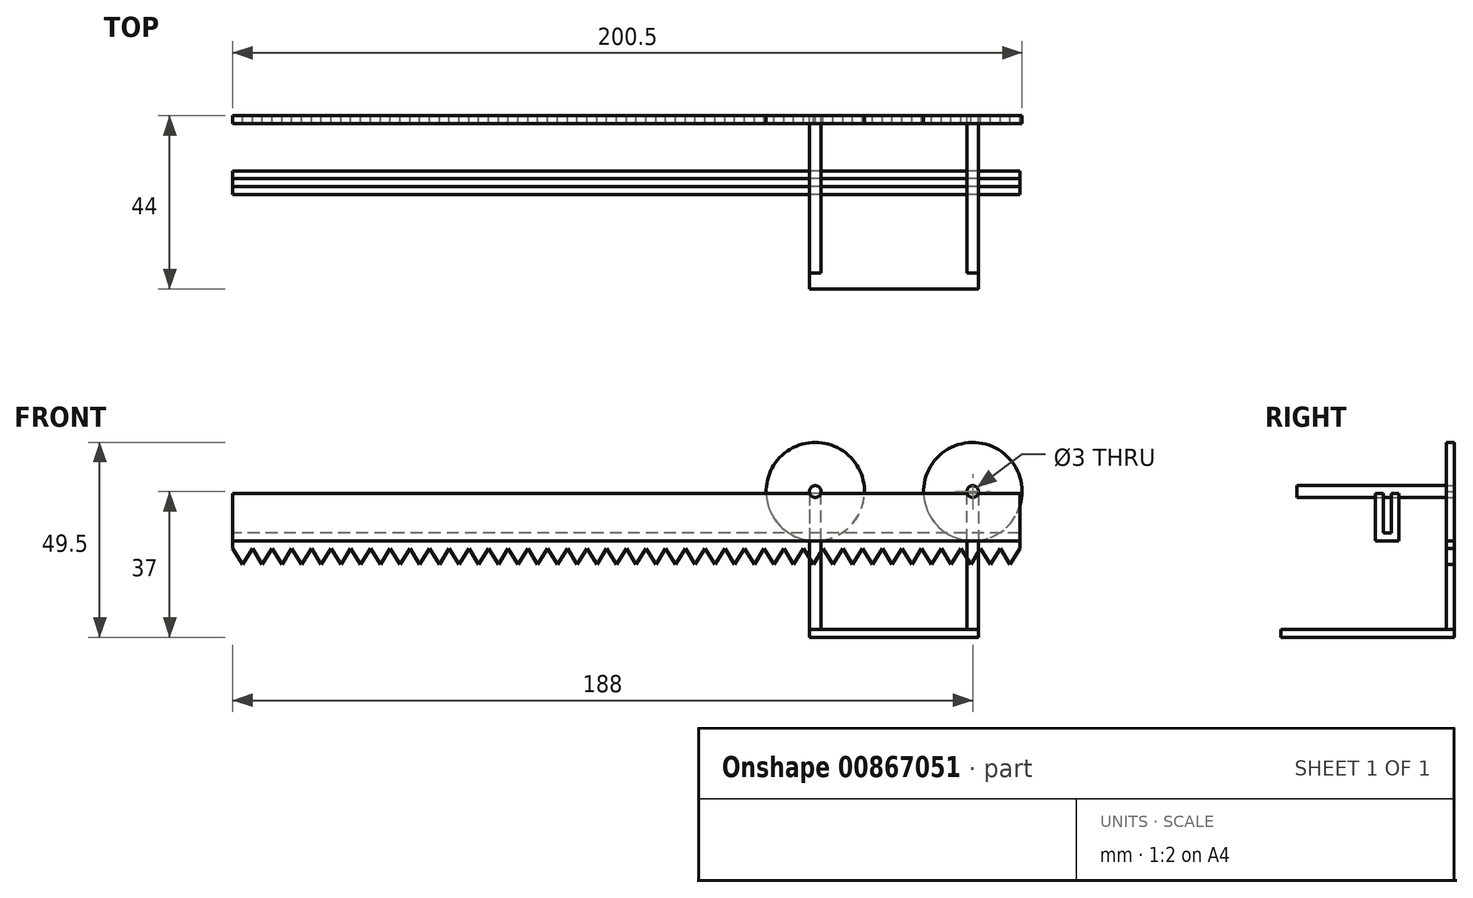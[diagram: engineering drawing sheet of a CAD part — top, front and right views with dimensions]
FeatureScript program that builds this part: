
annotation { "Feature Type Name" : "Feature", "Feature Type Description" : "" }
export const myFeature = defineFeature(function(context is Context, id is Id, definition is map)
    precondition{}
    {
        {
            assignVariable(context, id + "F0", {"name" : "Length", "anyValue" : 200});
        }
        {
            assignVariable(context, id + "F1", {"name" : "Width_Of_Cart", "anyValue" : 40});
        }
        {
            var Q0;
            Q0=qCreatedBy(makeId("Right.planeOp"),FACE);
            var sketch = newSketch(context, id + "F2", { "sketchPlane" : qUnion([Q0])});
            skLineSegment(sketch, "E0", {"start": v(-14, 0) * mm, "end": v(-14, 12) * mm});
            skLineSegment(sketch, "E1", {"start": v(-14, 12) * mm, "end": v(-16, 12) * mm});
            skLineSegment(sketch, "E2", {"start": v(-16, 12) * mm, "end": v(-16, 2) * mm});
            skLineSegment(sketch, "E3", {"start": v(-16, 2) * mm, "end": v(-18, 2) * mm});
            skLineSegment(sketch, "E4", {"start": v(-18, 2) * mm, "end": v(-18, 12) * mm});
            skLineSegment(sketch, "E5", {"start": v(-18, 12) * mm, "end": v(-20, 12) * mm});
            skLineSegment(sketch, "E6", {"start": v(-20, 12) * mm, "end": v(-20, 0) * mm});
            skLineSegment(sketch, "E7", {"start": v(-20, 0) * mm, "end": v(-14, 0) * mm});
            skLineSegment(sketch, "E8", {"start": v(-17, 2) * mm, "end": v(-17, 12) * mm, "construction": true});
            skLineSegment(sketch, "E9", {"start": v(0, 0.92) * mm, "end": v(0, 20.43) * mm, "construction": true});
            skSolve(sketch);
        }
        {
            var Q0;
            Q0 = qSketchRegion(id + "F2", true);
            extrude(context, id + "F3", {"entities" : qUnion([Q0]), "depth" : (getVariable(context, 'Length')) * mm, "offsetDistance" : 25 * mm, "symmetric" : true});
        }
        {
            var Q0;
            Q0=qCreatedBy(makeId("Front.planeOp"),FACE);
            var sketch = newSketch(context, id + "F4", { "sketchPlane" : qUnion([Q0])});
            skCircle(sketch, "E10", {"center": v(88, 12.5) * mm, "radius": 12.5 * mm});
            skLineSegment(sketch, "E11", {"start": v(68, 0) * mm, "end": v(68, 23.98) * mm, "construction": true});
            skCircle(sketch, "E12.MirrorC", {"center": v(48, 12.5) * mm, "radius": 12.5 * mm});
            skLineSegment(sketch, "E13", {"start": v(46.5, 12.5) * mm, "end": v(46.5, -22.5) * mm});
            skLineSegment(sketch, "E14", {"start": v(46.5, -22.5) * mm, "end": v(49.5, -22.5) * mm});
            skLineSegment(sketch, "E15", {"start": v(49.5, -22.5) * mm, "end": v(49.5, 12.5) * mm});
            skArc(sketch, "E16", {"start": v(49.5, 12.5) * mm, "mid": v(48, 14) * mm, "end": v(46.5, 12.5) * mm});
            skLineSegment(sketch, "E17.MirrorCS", {"start": v(86.5, -22.5) * mm, "end": v(86.5, 12.5) * mm});
            skArc(sketch, "E18.MirrorCS", {"start": v(86.5, 12.5) * mm, "mid": v(88, 14) * mm, "end": v(89.5, 12.5) * mm});
            skLineSegment(sketch, "E19.MirrorCS", {"start": v(89.5, -22.5) * mm, "end": v(86.5, -22.5) * mm});
            skLineSegment(sketch, "E20.MirrorCS", {"start": v(89.5, 12.5) * mm, "end": v(89.5, -22.5) * mm});
            skLineSegment(sketch, "E21", {"start": v(100, 0) * mm, "end": v(-100, 0) * mm});
            skLineSegment(sketch, "E22", {"start": v(100, 0) * mm, "end": v(100, -2) * mm});
            skLineSegment(sketch, "E23", {"start": v(100, -2) * mm, "end": v(97.5, -6) * mm});
            skLineSegment(sketch, "E24", {"start": v(97.5, -6) * mm, "end": v(95, -2) * mm});
            skLineSegment(sketch, "E25", {"start": v(97.5, -6) * mm, "end": v(97.5, -2) * mm, "construction": true});
            skLineSegment(sketch, "E26.1.0.0", {"start": v(92.5, -6) * mm, "end": v(90, -2) * mm});
            skLineSegment(sketch, "E26.1.0.1", {"start": v(95, -2) * mm, "end": v(92.5, -6) * mm});
            skLineSegment(sketch, "E26.2.0.0", {"start": v(87.5, -6) * mm, "end": v(85, -2) * mm});
            skLineSegment(sketch, "E26.2.0.1", {"start": v(90, -2) * mm, "end": v(87.5, -6) * mm});
            skLineSegment(sketch, "E26.3.0.0", {"start": v(82.5, -6) * mm, "end": v(80, -2) * mm});
            skLineSegment(sketch, "E26.3.0.1", {"start": v(85, -2) * mm, "end": v(82.5, -6) * mm});
            skLineSegment(sketch, "E26.4.0.0", {"start": v(77.5, -6) * mm, "end": v(75, -2) * mm});
            skLineSegment(sketch, "E26.4.0.1", {"start": v(80, -2) * mm, "end": v(77.5, -6) * mm});
            skLineSegment(sketch, "E26.5.0.0", {"start": v(72.5, -6) * mm, "end": v(70, -2) * mm});
            skLineSegment(sketch, "E26.5.0.1", {"start": v(75, -2) * mm, "end": v(72.5, -6) * mm});
            skLineSegment(sketch, "E26.6.0.0", {"start": v(67.5, -6) * mm, "end": v(65, -2) * mm});
            skLineSegment(sketch, "E26.6.0.1", {"start": v(70, -2) * mm, "end": v(67.5, -6) * mm});
            skLineSegment(sketch, "E26.7.0.0", {"start": v(62.5, -6) * mm, "end": v(60, -2) * mm});
            skLineSegment(sketch, "E26.7.0.1", {"start": v(65, -2) * mm, "end": v(62.5, -6) * mm});
            skLineSegment(sketch, "E26.8.0.0", {"start": v(57.5, -6) * mm, "end": v(55, -2) * mm});
            skLineSegment(sketch, "E26.8.0.1", {"start": v(60, -2) * mm, "end": v(57.5, -6) * mm});
            skLineSegment(sketch, "E26.9.0.0", {"start": v(52.5, -6) * mm, "end": v(50, -2) * mm});
            skLineSegment(sketch, "E26.9.0.1", {"start": v(55, -2) * mm, "end": v(52.5, -6) * mm});
            skLineSegment(sketch, "E26.10.0.0", {"start": v(47.5, -6) * mm, "end": v(45, -2) * mm});
            skLineSegment(sketch, "E26.10.0.1", {"start": v(50, -2) * mm, "end": v(47.5, -6) * mm});
            skLineSegment(sketch, "E26.11.0.0", {"start": v(42.5, -6) * mm, "end": v(40, -2) * mm});
            skLineSegment(sketch, "E26.11.0.1", {"start": v(45, -2) * mm, "end": v(42.5, -6) * mm});
            skLineSegment(sketch, "E26.12.0.0", {"start": v(37.5, -6) * mm, "end": v(35, -2) * mm});
            skLineSegment(sketch, "E26.12.0.1", {"start": v(40, -2) * mm, "end": v(37.5, -6) * mm});
            skLineSegment(sketch, "E26.13.0.0", {"start": v(32.5, -6) * mm, "end": v(30, -2) * mm});
            skLineSegment(sketch, "E26.13.0.1", {"start": v(35, -2) * mm, "end": v(32.5, -6) * mm});
            skLineSegment(sketch, "E26.14.0.0", {"start": v(27.5, -6) * mm, "end": v(25, -2) * mm});
            skLineSegment(sketch, "E26.14.0.1", {"start": v(30, -2) * mm, "end": v(27.5, -6) * mm});
            skLineSegment(sketch, "E26.15.0.0", {"start": v(22.5, -6) * mm, "end": v(20, -2) * mm});
            skLineSegment(sketch, "E26.15.0.1", {"start": v(25, -2) * mm, "end": v(22.5, -6) * mm});
            skLineSegment(sketch, "E26.16.0.0", {"start": v(17.5, -6) * mm, "end": v(15, -2) * mm});
            skLineSegment(sketch, "E26.16.0.1", {"start": v(20, -2) * mm, "end": v(17.5, -6) * mm});
            skLineSegment(sketch, "E26.17.0.0", {"start": v(12.5, -6) * mm, "end": v(10, -2) * mm});
            skLineSegment(sketch, "E26.17.0.1", {"start": v(15, -2) * mm, "end": v(12.5, -6) * mm});
            skLineSegment(sketch, "E26.18.0.0", {"start": v(7.5, -6) * mm, "end": v(5, -2) * mm});
            skLineSegment(sketch, "E26.18.0.1", {"start": v(10, -2) * mm, "end": v(7.5, -6) * mm});
            skLineSegment(sketch, "E26.19.0.0", {"start": v(2.5, -6) * mm, "end": v(0, -2) * mm});
            skLineSegment(sketch, "E26.19.0.1", {"start": v(5, -2) * mm, "end": v(2.5, -6) * mm});
            skLineSegment(sketch, "E26.20.0.0", {"start": v(-2.5, -6) * mm, "end": v(-5, -2) * mm});
            skLineSegment(sketch, "E26.20.0.1", {"start": v(0, -2) * mm, "end": v(-2.5, -6) * mm});
            skLineSegment(sketch, "E26.21.0.0", {"start": v(-7.5, -6) * mm, "end": v(-10, -2) * mm});
            skLineSegment(sketch, "E26.21.0.1", {"start": v(-5, -2) * mm, "end": v(-7.5, -6) * mm});
            skLineSegment(sketch, "E26.22.0.0", {"start": v(-12.5, -6) * mm, "end": v(-15, -2) * mm});
            skLineSegment(sketch, "E26.22.0.1", {"start": v(-10, -2) * mm, "end": v(-12.5, -6) * mm});
            skLineSegment(sketch, "E26.23.0.0", {"start": v(-17.5, -6) * mm, "end": v(-20, -2) * mm});
            skLineSegment(sketch, "E26.23.0.1", {"start": v(-15, -2) * mm, "end": v(-17.5, -6) * mm});
            skLineSegment(sketch, "E26.24.0.0", {"start": v(-22.5, -6) * mm, "end": v(-25, -2) * mm});
            skLineSegment(sketch, "E26.24.0.1", {"start": v(-20, -2) * mm, "end": v(-22.5, -6) * mm});
            skLineSegment(sketch, "E26.25.0.0", {"start": v(-27.5, -6) * mm, "end": v(-30, -2) * mm});
            skLineSegment(sketch, "E26.25.0.1", {"start": v(-25, -2) * mm, "end": v(-27.5, -6) * mm});
            skLineSegment(sketch, "E26.26.0.0", {"start": v(-32.5, -6) * mm, "end": v(-35, -2) * mm});
            skLineSegment(sketch, "E26.26.0.1", {"start": v(-30, -2) * mm, "end": v(-32.5, -6) * mm});
            skLineSegment(sketch, "E26.27.0.0", {"start": v(-37.5, -6) * mm, "end": v(-40, -2) * mm});
            skLineSegment(sketch, "E26.27.0.1", {"start": v(-35, -2) * mm, "end": v(-37.5, -6) * mm});
            skLineSegment(sketch, "E26.28.0.0", {"start": v(-42.5, -6) * mm, "end": v(-45, -2) * mm});
            skLineSegment(sketch, "E26.28.0.1", {"start": v(-40, -2) * mm, "end": v(-42.5, -6) * mm});
            skLineSegment(sketch, "E26.29.0.0", {"start": v(-47.5, -6) * mm, "end": v(-50, -2) * mm});
            skLineSegment(sketch, "E26.29.0.1", {"start": v(-45, -2) * mm, "end": v(-47.5, -6) * mm});
            skLineSegment(sketch, "E26.30.0.0", {"start": v(-52.5, -6) * mm, "end": v(-55, -2) * mm});
            skLineSegment(sketch, "E26.30.0.1", {"start": v(-50, -2) * mm, "end": v(-52.5, -6) * mm});
            skLineSegment(sketch, "E26.31.0.0", {"start": v(-57.5, -6) * mm, "end": v(-60, -2) * mm});
            skLineSegment(sketch, "E26.31.0.1", {"start": v(-55, -2) * mm, "end": v(-57.5, -6) * mm});
            skLineSegment(sketch, "E26.32.0.0", {"start": v(-62.5, -6) * mm, "end": v(-65, -2) * mm});
            skLineSegment(sketch, "E26.32.0.1", {"start": v(-60, -2) * mm, "end": v(-62.5, -6) * mm});
            skLineSegment(sketch, "E26.33.0.0", {"start": v(-67.5, -6) * mm, "end": v(-70, -2) * mm});
            skLineSegment(sketch, "E26.33.0.1", {"start": v(-65, -2) * mm, "end": v(-67.5, -6) * mm});
            skLineSegment(sketch, "E26.34.0.0", {"start": v(-72.5, -6) * mm, "end": v(-75, -2) * mm});
            skLineSegment(sketch, "E26.34.0.1", {"start": v(-70, -2) * mm, "end": v(-72.5, -6) * mm});
            skLineSegment(sketch, "E26.35.0.0", {"start": v(-77.5, -6) * mm, "end": v(-80, -2) * mm});
            skLineSegment(sketch, "E26.35.0.1", {"start": v(-75, -2) * mm, "end": v(-77.5, -6) * mm});
            skLineSegment(sketch, "E26.36.0.0", {"start": v(-82.5, -6) * mm, "end": v(-85, -2) * mm});
            skLineSegment(sketch, "E26.36.0.1", {"start": v(-80, -2) * mm, "end": v(-82.5, -6) * mm});
            skLineSegment(sketch, "E26.37.0.0", {"start": v(-87.5, -6) * mm, "end": v(-90, -2) * mm});
            skLineSegment(sketch, "E26.37.0.1", {"start": v(-85, -2) * mm, "end": v(-87.5, -6) * mm});
            skLineSegment(sketch, "E26.38.0.0", {"start": v(-92.5, -6) * mm, "end": v(-95, -2) * mm});
            skLineSegment(sketch, "E26.38.0.1", {"start": v(-90, -2) * mm, "end": v(-92.5, -6) * mm});
            skLineSegment(sketch, "E26.39.0.0", {"start": v(-97.5, -6) * mm, "end": v(-100, -2) * mm});
            skLineSegment(sketch, "E26.39.0.1", {"start": v(-95, -2) * mm, "end": v(-97.5, -6) * mm});
            skLineSegment(sketch, "E26.direction1", {"start": v(97.5, -6) * mm, "end": v(92.5, -6) * mm, "construction": true});
            skLineSegment(sketch, "E27", {"start": v(-100, -2) * mm, "end": v(-100, 0) * mm});
            skCircle(sketch, "E28", {"center": v(88, 12.5) * mm, "radius": 1.5 * mm});
            skCircle(sketch, "E29", {"center": v(48, 12.5) * mm, "radius": 1.5 * mm});
            skSolve(sketch);
        }
        {
            var Q0;
            {var subQ0=sQuery(id+"F4.wireOp",EDGE,"E17.MirrorCS");var subQ1=sQuery(id+"F4.wireOp",EDGE,"E10");var subQ2=makeQuery(id+"F4.imprint","INTERSECT",VERTEX,{"derivedFrom":[subQ1,subQ0]});Q0=makeQuery(id+"F4.imprint","IMPRINT",FACE,{"disambiguationData":[TD([[makeQuery(id+"F4.imprint","IMPRINT",EDGE,{"disambiguationData":[TD([[subQ2,1.0]])],"derivedFrom":subQ1}),1.0]])]});}
            var Q1;
            {var subQ4=sQuery(id+"F4.wireOp",EDGE,"E10");var subQ6=sQuery(id+"F4.wireOp",EDGE,"E17.MirrorCS");var subQ7=makeQuery(id+"F4.imprint","INTERSECT",VERTEX,{"derivedFrom":[subQ4,subQ6]});Q1=makeQuery(id+"F4.imprint","IMPRINT",FACE,{"disambiguationData":[TD([[makeQuery(id+"F4.imprint","IMPRINT",EDGE,{"disambiguationData":[TD([[subQ7,-1.0]])],"derivedFrom":subQ4}),1.0]])]});}
            var Q2;
            {var subQ0=sQuery(id+"F4.wireOp",EDGE,"E15");var subQ1=sQuery(id+"F4.wireOp",EDGE,"E12.MirrorC");var subQ2=makeQuery(id+"F4.imprint","INTERSECT",VERTEX,{"derivedFrom":[subQ1,subQ0]});Q2=makeQuery(id+"F4.imprint","IMPRINT",FACE,{"disambiguationData":[TD([[makeQuery(id+"F4.imprint","IMPRINT",EDGE,{"disambiguationData":[TD([[subQ2,1.0]])],"derivedFrom":subQ1}),-1.0]])]});}
            var Q3;
            {var subQ4=sQuery(id+"F4.wireOp",EDGE,"E12.MirrorC");var subQ6=sQuery(id+"F4.wireOp",EDGE,"E15");var subQ8=makeQuery(id+"F4.imprint","INTERSECT",VERTEX,{"derivedFrom":[subQ4,subQ6]});Q3=makeQuery(id+"F4.imprint","IMPRINT",FACE,{"disambiguationData":[TD([[makeQuery(id+"F4.imprint","IMPRINT",EDGE,{"disambiguationData":[TD([[subQ8,-1.0]])],"derivedFrom":subQ4}),-1.0]])]});}
            var Q4;
            Q4=makeQuery(id+"F3.opExtrude","SWEPT_FACE",FACE,{"disambiguationData":[OSD([sQuery(id+"F2.wireOp",EDGE,"E2")])]});
            extrude(context, id + "F5", {"entities" : qUnion([Q0, Q1, Q2, Q3]), "depth" : 2 * mm, "endBoundEntityFace" : qUnion([Q4]), "hasOffset" : true, "offsetDistance" : 12 * mm});
        }
        {
            var Q0;
            Q0=makeQuery(id+"F4.imprint","IMPRINT",FACE,{"disambiguationData":[TD([[makeQuery(id+"F4.imprint","IMPRINT",EDGE,{"derivedFrom":sQuery(id+"F4.wireOp",EDGE,"E26.3.0.0")}),-1.0]])]});
            var Q1;
            {var subQ8=sQuery(id+"F4.wireOp",EDGE,"E26.2.0.1");Q1=makeQuery(id+"F4.imprint","IMPRINT",FACE,{"disambiguationData":[TD([[makeQuery(id+"F4.imprint","IMPRINT",EDGE,{"derivedFrom":subQ8}),-1.0]])]});}
            var Q2;
            {var subQ0=sQuery(id+"F4.wireOp",EDGE,"E22");Q2=makeQuery(id+"F4.imprint","IMPRINT",FACE,{"disambiguationData":[TD([[makeQuery(id+"F4.imprint","IMPRINT",EDGE,{"derivedFrom":subQ0}),-1.0]])]});}
            var Q3;
            Q3=makeQuery(id+"F4.imprint","IMPRINT",FACE,{"disambiguationData":[TD([[makeQuery(id+"F4.imprint","IMPRINT",EDGE,{"derivedFrom":sQuery(id+"F4.wireOp",EDGE,"E26.9.0.0")}),-1.0]])]});
            var Q4;
            {var subQ8=sQuery(id+"F4.wireOp",EDGE,"E26.8.0.1");Q4=makeQuery(id+"F4.imprint","IMPRINT",FACE,{"disambiguationData":[TD([[makeQuery(id+"F4.imprint","IMPRINT",EDGE,{"derivedFrom":subQ8}),-1.0]])]});}
            var Q5;
            Q5=makeQuery(id+"F4.imprint","IMPRINT",FACE,{"disambiguationData":[TD([[makeQuery(id+"F4.imprint","IMPRINT",EDGE,{"derivedFrom":sQuery(id+"F4.wireOp",EDGE,"E26.11.0.0")}),-1.0]])]});
            var Q6;
            {var subQ0=sQuery(id+"F4.wireOp",EDGE,"E21");var subQ1=sQuery(id+"F4.wireOp",EDGE,"E13");var subQ2=makeQuery(id+"F4.imprint","INTERSECT",VERTEX,{"derivedFrom":[subQ1,subQ0]});Q6=makeQuery(id+"F4.imprint","IMPRINT",FACE,{"disambiguationData":[TD([[makeQuery(id+"F4.imprint","IMPRINT",EDGE,{"disambiguationData":[TD([[subQ2,-1.0]])],"derivedFrom":subQ1}),1.0]])]});}
            extrude(context, id + "F6", {"entities" : qUnion([Q0, Q1, Q2, Q3, Q4, Q5, Q6]), "depth" : 2 * mm, "offsetDistance" : 25 * mm});
        }
        {
            var Q0;
            {var subQ6=sQuery(id+"F4.wireOp",EDGE,"E19.MirrorCS");Q0=makeQuery(id+"F4.imprint","IMPRINT",FACE,{"disambiguationData":[TD([[makeQuery(id+"F4.imprint","IMPRINT",EDGE,{"derivedFrom":subQ6}),-1.0]])]});}
            var Q1;
            {var subQ5=sQuery(id+"F4.wireOp",EDGE,"E26.2.0.0");var subQ7=sQuery(id+"F4.wireOp",EDGE,"E17.MirrorCS");var subQ8=makeQuery(id+"F4.imprint","INTERSECT",VERTEX,{"derivedFrom":[subQ7,subQ5]});Q1=makeQuery(id+"F4.imprint","IMPRINT",FACE,{"disambiguationData":[TD([[makeQuery(id+"F4.imprint","IMPRINT",EDGE,{"disambiguationData":[TD([[subQ8,-1.0]])],"derivedFrom":subQ7}),-1.0]])]});}
            var Q2;
            {var subQ1=sQuery(id+"F4.wireOp",EDGE,"E17.MirrorCS");var subQ3=sQuery(id+"F4.wireOp",EDGE,"E10");var subQ4=makeQuery(id+"F4.imprint","INTERSECT",VERTEX,{"derivedFrom":[subQ3,subQ1]});Q2=makeQuery(id+"F4.imprint","IMPRINT",FACE,{"disambiguationData":[TD([[makeQuery(id+"F4.imprint","IMPRINT",EDGE,{"disambiguationData":[TD([[subQ4,-1.0]])],"derivedFrom":subQ3}),1.0]])]});}
            var Q3;
            {var subQ0=sQuery(id+"F4.wireOp",EDGE,"E28");var subQ1=makeQuery(id+"F4.imprint","INTERSECT",VERTEX,{"derivedFrom":[sQuery(id+"F4.wireOp",EDGE,"E17.MirrorCS"),subQ0]});Q3=makeQuery(id+"F4.imprint","IMPRINT",FACE,{"disambiguationData":[TD([[makeQuery(id+"F4.imprint","IMPRINT",EDGE,{"disambiguationData":[TD([[subQ1,1.0]])],"derivedFrom":subQ0}),1.0]])]});}
            var Q4;
            {var subQ0=sQuery(id+"F4.wireOp",EDGE,"E29");var subQ1=makeQuery(id+"F4.imprint","INTERSECT",VERTEX,{"derivedFrom":[sQuery(id+"F4.wireOp",EDGE,"E13"),subQ0]});Q4=makeQuery(id+"F4.imprint","IMPRINT",FACE,{"disambiguationData":[TD([[makeQuery(id+"F4.imprint","IMPRINT",EDGE,{"disambiguationData":[TD([[subQ1,1.0]])],"derivedFrom":subQ0}),1.0]])]});}
            var Q5;
            {var subQ3=sQuery(id+"F4.wireOp",EDGE,"E12.MirrorC");var subQ5=sQuery(id+"F4.wireOp",EDGE,"E15");var subQ7=makeQuery(id+"F4.imprint","INTERSECT",VERTEX,{"derivedFrom":[subQ3,subQ5]});Q5=makeQuery(id+"F4.imprint","IMPRINT",FACE,{"disambiguationData":[TD([[makeQuery(id+"F4.imprint","IMPRINT",EDGE,{"disambiguationData":[TD([[subQ7,-1.0]])],"derivedFrom":subQ3}),-1.0]])]});}
            var Q6;
            {var subQ0=sQuery(id+"F4.wireOp",EDGE,"E21");var subQ1=sQuery(id+"F4.wireOp",EDGE,"E13");var subQ2=makeQuery(id+"F4.imprint","INTERSECT",VERTEX,{"derivedFrom":[subQ1,subQ0]});Q6=makeQuery(id+"F4.imprint","IMPRINT",FACE,{"disambiguationData":[TD([[makeQuery(id+"F4.imprint","IMPRINT",EDGE,{"disambiguationData":[TD([[subQ2,-1.0]])],"derivedFrom":subQ1}),1.0]])]});}
            var Q7;
            {var subQ1=sQuery(id+"F4.wireOp",EDGE,"E14");Q7=makeQuery(id+"F4.imprint","IMPRINT",FACE,{"disambiguationData":[TD([[makeQuery(id+"F4.imprint","IMPRINT",EDGE,{"derivedFrom":subQ1}),1.0]])]});}
            var Q8;
            {var subQ0=sQuery(id+"F4.wireOp",EDGE,"E20.MirrorCS");var subQ1=sQuery(id+"F4.wireOp",EDGE,"E10");var subQ2=makeQuery(id+"F4.imprint","INTERSECT",VERTEX,{"derivedFrom":[subQ1,subQ0]});Q8=makeQuery(id+"F4.imprint","IMPRINT",FACE,{"disambiguationData":[TD([[makeQuery(id+"F4.imprint","IMPRINT",EDGE,{"disambiguationData":[TD([[subQ2,1.0]])],"derivedFrom":subQ1}),-1.0]])]});}
            var Q9;
            {var subQ0=sQuery(id+"F4.wireOp",EDGE,"E17.MirrorCS");var subQ1=sQuery(id+"F4.wireOp",EDGE,"E10");var subQ2=makeQuery(id+"F4.imprint","INTERSECT",VERTEX,{"derivedFrom":[subQ1,subQ0]});Q9=makeQuery(id+"F4.imprint","IMPRINT",FACE,{"disambiguationData":[TD([[makeQuery(id+"F4.imprint","IMPRINT",EDGE,{"disambiguationData":[TD([[subQ2,-1.0]])],"derivedFrom":subQ1}),-1.0]])]});}
            var Q10;
            {var subQ0=sQuery(id+"F4.wireOp",EDGE,"E15");var subQ1=sQuery(id+"F4.wireOp",EDGE,"E12.MirrorC");var subQ2=makeQuery(id+"F4.imprint","INTERSECT",VERTEX,{"derivedFrom":[subQ1,subQ0]});Q10=makeQuery(id+"F4.imprint","IMPRINT",FACE,{"disambiguationData":[TD([[makeQuery(id+"F4.imprint","IMPRINT",EDGE,{"disambiguationData":[TD([[subQ2,-1.0]])],"derivedFrom":subQ1}),1.0]])]});}
            var Q11;
            {var subQ0=sQuery(id+"F4.wireOp",EDGE,"E13");var subQ1=sQuery(id+"F4.wireOp",EDGE,"E12.MirrorC");var subQ2=makeQuery(id+"F4.imprint","INTERSECT",VERTEX,{"derivedFrom":[subQ1,subQ0]});Q11=makeQuery(id+"F4.imprint","IMPRINT",FACE,{"disambiguationData":[TD([[makeQuery(id+"F4.imprint","IMPRINT",EDGE,{"disambiguationData":[TD([[subQ2,1.0]])],"derivedFrom":subQ1}),1.0]])]});}
            extrude(context, id + "F7", {"entities" : qUnion([Q0, Q1, Q2, Q3, Q4, Q5, Q6, Q7, Q8, Q9, Q10, Q11]), "depth" : 2 * mm, "offsetDistance" : 25 * mm});
        }
        {
            var Q0;
            {var subQ0=sQuery(id+"F4.wireOp",EDGE,"E28");var subQ1=makeQuery(id+"F4.imprint","INTERSECT",VERTEX,{"derivedFrom":[sQuery(id+"F4.wireOp",EDGE,"E17.MirrorCS"),subQ0]});Q0=makeQuery(id+"F4.imprint","IMPRINT",FACE,{"disambiguationData":[TD([[makeQuery(id+"F4.imprint","IMPRINT",EDGE,{"disambiguationData":[TD([[subQ1,1.0]])],"derivedFrom":subQ0}),1.0]])]});}
            var Q1;
            {var subQ0=sQuery(id+"F4.wireOp",EDGE,"E29");var subQ1=makeQuery(id+"F4.imprint","INTERSECT",VERTEX,{"derivedFrom":[sQuery(id+"F4.wireOp",EDGE,"E13"),subQ0]});Q1=makeQuery(id+"F4.imprint","IMPRINT",FACE,{"disambiguationData":[TD([[makeQuery(id+"F4.imprint","IMPRINT",EDGE,{"disambiguationData":[TD([[subQ1,1.0]])],"derivedFrom":subQ0}),1.0]])]});}
            extrude(context, id + "F8", {"entities" : qUnion([Q0, Q1]), "depth" : (getVariable(context, 'Width_Of_Cart')) * mm, "offsetDistance" : 25 * mm});
        }
        {
            var Q0;
            Q0=makeQuery(id+"F7.opExtrude","SWEPT_FACE",FACE,{"disambiguationData":[OSD([sQuery(id+"F4.wireOp",EDGE,"E19.MirrorCS")])]});
            var sketch = newSketch(context, id + "F9", { "sketchPlane" : qUnion([Q0])});
            skLineSegment(sketch, "E30.bottom", {"start": v(89.5, 0) * mm, "end": v(46.5, 0) * mm});
            skLineSegment(sketch, "E30.top", {"start": v(89.5, 44) * mm, "end": v(46.5, 44) * mm});
            skLineSegment(sketch, "E30.left", {"start": v(89.5, 0) * mm, "end": v(89.5, 44) * mm});
            skLineSegment(sketch, "E30.right", {"start": v(46.5, 0) * mm, "end": v(46.5, 44) * mm});
            skSolve(sketch);
        }
        {
            var Q0;
            Q0 = qSketchRegion(id + "F9", true);
            extrude(context, id + "F10", {"entities" : qUnion([Q0]), "depth" : 2 * mm, "offsetDistance" : 25 * mm});
        }
    });
